# Revit family: CARLO CYLINDER LIGHT Pendant_ Surface
name_source: partatom
category: Lighting Fixtures
units: mm (PartAtom-declared; Revit-internal decimal feet)

## family parameters
Cut with Voids When Loaded = No
Host = Face
Light Source = Yes
Part Type = Normal
Room Calculation Point = No
Round Connector Dimension = Use Diameter
Shared = No

## types (12) — shared parameters
Average life based on 104F(HRS) = L70 - 100,000 Hours
CRI = 90Ra
Color Filter = 16777215
Default Elevation = 0' - 0"
Description = This architectural Carlo Cylinder light is designed for accent lighting and features a state-of-the-art design. 
IP65 rated for wet locations.
Dimming / Control = 0-10V
Dimming Lamp Color Temperature Shift = <None>
Finish/Color = BLACK
IP Rating = IP 65 Suitable for Wet Location
Load Classification = Lighting
Manufacturer = Above All Lighting
Pendant Rod Length = 4' - 0 7/16"
Power Factor = 1
Tilt Angle = -90.00°
Type Comments = CARLO CYLINDER LIGHT
CARLO CYLINDER LIGHT Pendant/Surface
URL = https://www.abovealllighting.com

## per-type parameters (varying)
| type | Apparent Load | BEAMING ANGLE | Fixture Diameter | Fixture Height | Model | Photometric Web File | Size 04 | Size 08 | Wattage Comments |
| CCL4-07-20SPSW8-25-PSM-BK | 20 VA | 25.00° | 0' - 4" | 0' - 7 3/16" | CCL4-07-20SPSW8-25-PSM-BK | CCL4_20W_2700K_25__.IES | Yes | No | 12W/16W/20W |
| CCL4-07-20SPSW8-40-PSM-BK | 20 VA | 40.00° | 0' - 4" | 0' - 7 3/16" | CCL4-07-20SP2700K8-40-PSM-BK | CCL4_20W_2700K_40__.IES | Yes | No | 12W/16W/20W |
| CCL4-07-20SPSW8-60-PSM-BK | 20 VA | 60.00° | 0' - 4" | 0' - 7 3/16" | CCL4-07-20SPSW8-60-PSM-BK | CCL4_20W_5000K_60__.IES | Yes | No | 12W/16W/20W |
| CCL4-12-20SPSW8-25-PSM-BK | 20 VA | 25.00° | 0' - 4" | 1' - 0" | CCL4-12-20SPSW8-25-PSM-BK | CCL4_20W_2700K_25__.IES | Yes | No | 12W/16W/20W |
| CCL4-12-20SPSW8-40-PSM-BK | 20 VA | 40.00° | 0' - 4" | 1' - 0" | CCL4-12-20SPSW8-40-PSM-BK | CCL4_20W_2700K_40__.IES | Yes | No | 12W/16W/20W |
| CCL4-12-20SPSW8-60-PSM-BK | 20 VA | 60.00° | 0' - 4" | 1' - 0" | CCL4-12-20SPSW8-60-PSM-BK | CCL4_20W_5000K_60__.IES | Yes | No | 12W/16W/20W |
| CCL6-08-30SPSW8-25-PSM-BK | 30 VA | 25.00° | 0' - 6" | 0' - 8 11/16" | CCL6-08-30SPSW8-25-PSM-BK | CCL6_30W_2700K_25__.IES | No | Yes | 18W/24W/30W |
| CCL6-08-30SPSW8-60-PSM-BK | 30 VA | 60.00° | 0' - 6" | 0' - 8 11/16" | CCL6-08-30SPSW8-60-PSM-BK | CCL6_30W_2700K_60__.IES | No | Yes | 18W/24W/30W |
| CCL6-08-30SPSW8-40-PSM-BK | 30 VA | 40.00° | 0' - 6" | 0' - 8 11/16" | CCL6-08-30SPSW8-40-PSM-BK | CCL6_30W_3000K_40__.IES | No | Yes | 18W/24W/30W |
| CCL3-06-10SPSW8-25-PSM-BK | 10 VA | 25.00° | 0' - 3" | 0' - 6 3/16" | CCL3-06-10SPSW8-25-PSM-BK | CCL3 10W 3000K 25° (up and down light).IES | No | Yes | 6W/8W/10W |
| CCL3-06-10SPSW8-40-PSM-BK | 10 VA | 40.00° | 0' - 3" | 0' - 6 3/16" | CCL3-06-10SPSW8-40-PSM-BK | CCL3_10W_3000K_40__.IES | No | Yes | 6W/8W/10W |
| CCL3-06-10SPSW8-60-PSM-BK | 10 VA | 60.00° | 0' - 3" | 0' - 6 3/16" | CCL3-06-10SPSW8-60-PSM-BK | CCL3 10W 3000K 60° (up and down light).IES | No | Yes | 6W/8W/10W |

## geometry (parser evidence)
native form markers: Sweep x10
no freeform markers — native parametric forms only
